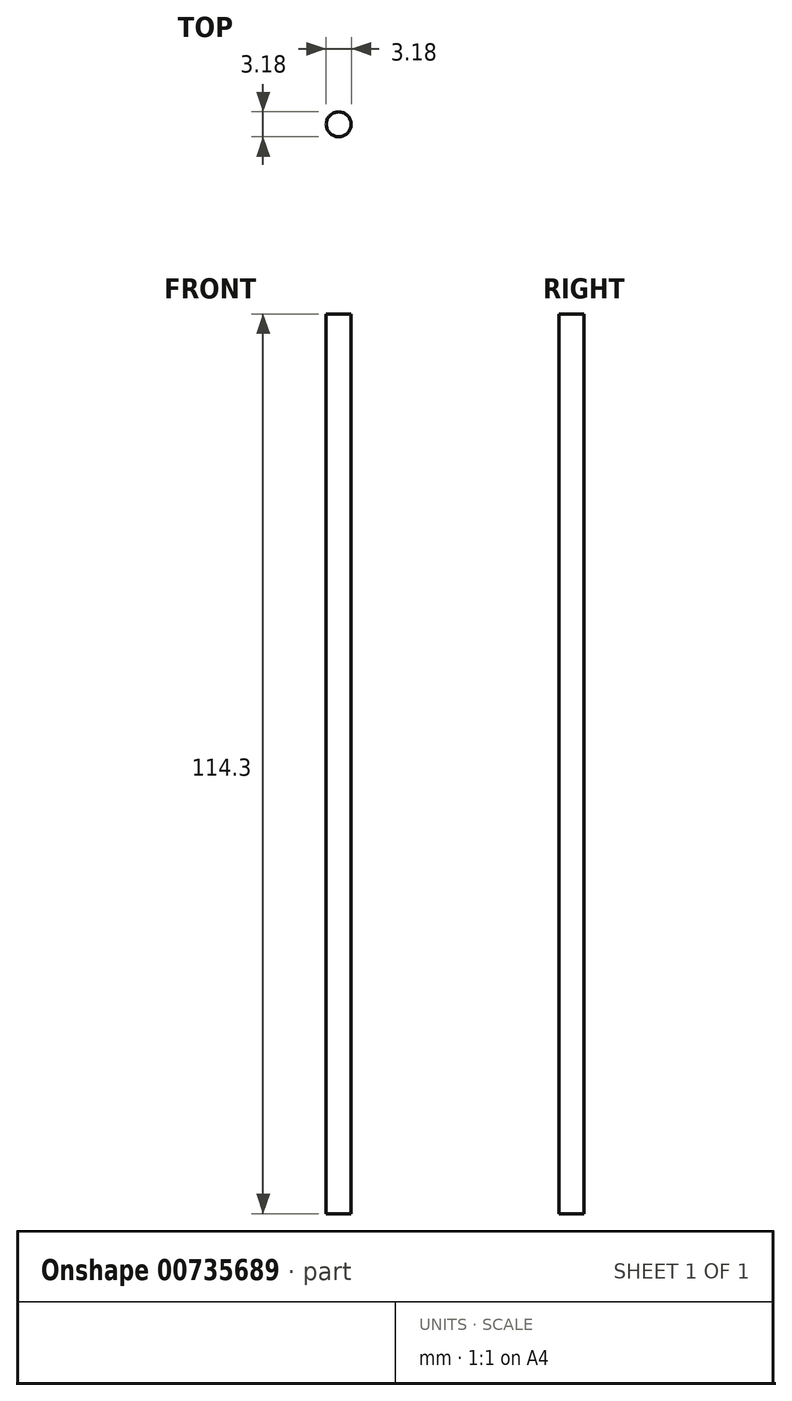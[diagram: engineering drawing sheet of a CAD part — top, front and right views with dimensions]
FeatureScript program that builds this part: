
annotation { "Feature Type Name" : "Feature", "Feature Type Description" : "" }
export const myFeature = defineFeature(function(context is Context, id is Id, definition is map)
    precondition{}
    {
        {
            var Q0;
            Q0=qCreatedBy(makeId("Top.planeOp"),FACE);
            var sketch = newSketch(context, id + "F0", { "sketchPlane" : qUnion([Q0])});
            skCircle(sketch, "E0", {"center": v(-106.8, -20.18) * mm, "radius": 1.59 * mm});
            skSolve(sketch);
        }
        {
            var Q0;
            Q0 = qSketchRegion(id + "F0", true);
            extrude(context, id + "F1", {"entities" : qUnion([Q0]), "depth" : 114.3 * mm, "offsetDistance" : 25.4 * mm});
        }
    });
